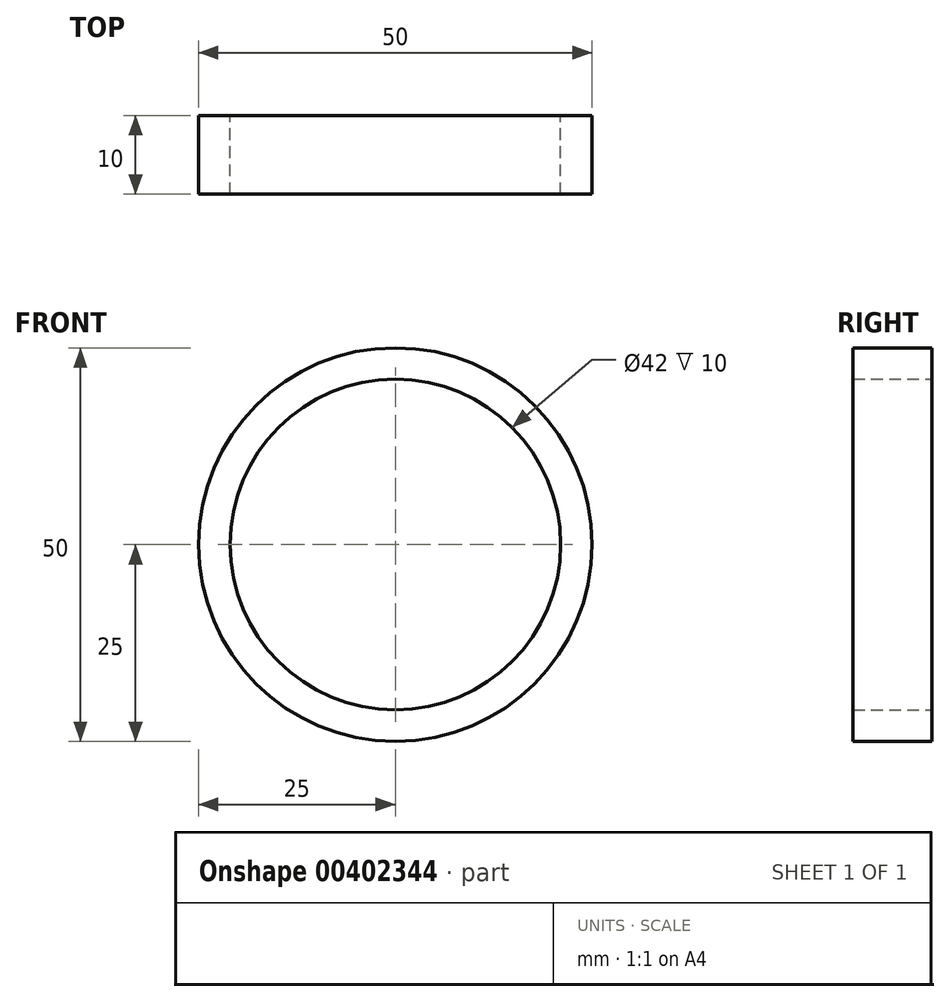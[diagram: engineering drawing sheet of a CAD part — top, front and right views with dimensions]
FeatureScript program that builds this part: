
annotation { "Feature Type Name" : "Feature", "Feature Type Description" : "" }
export const myFeature = defineFeature(function(context is Context, id is Id, definition is map)
    precondition{}
    {
        {
            var Q0;
            Q0=qCreatedBy(makeId("Front.planeOp"),FACE);
            var sketch = newSketch(context, id + "F0", { "sketchPlane" : qUnion([Q0])});
            skCircle(sketch, "E0", {"center": v(0, 0) * mm, "radius": 25 * mm});
            skCircle(sketch, "E1", {"center": v(0, 0) * mm, "radius": 21 * mm});
            skCircle(sketch, "E2", {"center": v(0, 0) * mm, "radius": 15 * mm});
            skSolve(sketch);
        }
        {
            var Q0;
            Q0=makeQuery(id+"F0.imprint","IMPRINT",FACE,{"disambiguationData":[TD([[makeQuery(id+"F0.imprint","IMPRINT",EDGE,{"derivedFrom":sQuery(id+"F0.wireOp",EDGE,"E0")}),1.0]])]});
            extrude(context, id + "F1", {"entities" : qUnion([Q0]), "endBound" : BoundingType.SYMMETRIC, "depth" : 10 * mm});
        }
    });
